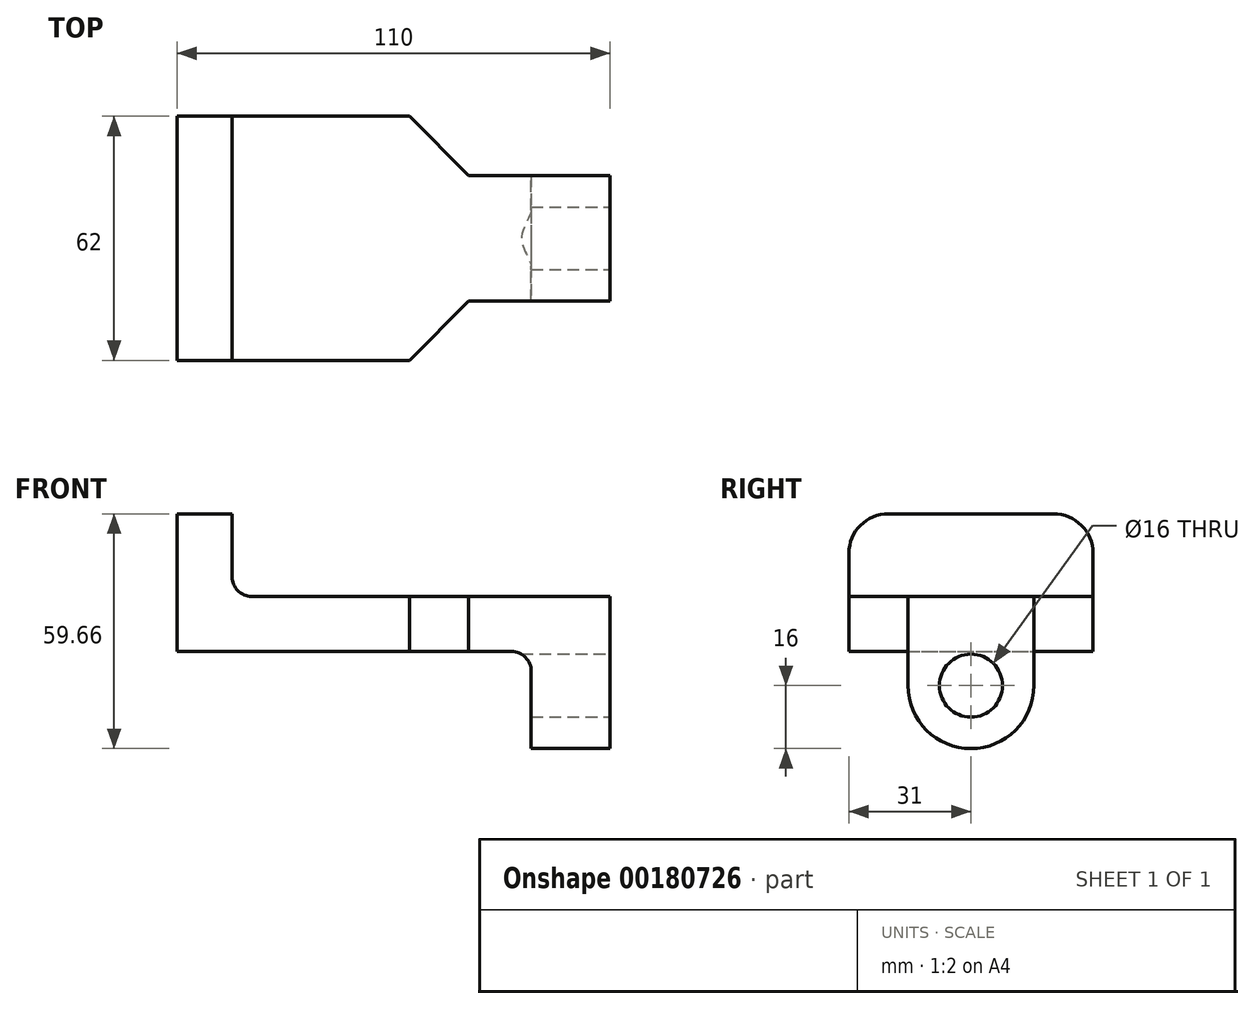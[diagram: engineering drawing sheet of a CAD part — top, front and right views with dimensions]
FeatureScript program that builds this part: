
annotation { "Feature Type Name" : "Feature", "Feature Type Description" : "" }
export const myFeature = defineFeature(function(context is Context, id is Id, definition is map)
    precondition{}
    {
        {
            var Q0;
            Q0=qCreatedBy(makeId("Front.planeOp"),FACE);
            var sketch = newSketch(context, id + "F0", { "sketchPlane" : qUnion([Q0])});
            skLineSegment(sketch, "E0", {"start": v(-90, 67.66) * mm, "end": v(-76, 67.66) * mm});
            skLineSegment(sketch, "E1", {"start": v(-76, 67.66) * mm, "end": v(-76, 46.66) * mm});
            skLineSegment(sketch, "E2", {"start": v(-76, 46.66) * mm, "end": v(20, 46.66) * mm});
            skLineSegment(sketch, "E3", {"start": v(20, 46.66) * mm, "end": v(20, 8) * mm});
            skLineSegment(sketch, "E4", {"start": v(20, 8) * mm, "end": v(0, 8) * mm});
            skLineSegment(sketch, "E5", {"start": v(0, 8) * mm, "end": v(0, 32.66) * mm});
            skLineSegment(sketch, "E6", {"start": v(0, 32.66) * mm, "end": v(-90, 32.66) * mm});
            skLineSegment(sketch, "E7", {"start": v(-90, 32.66) * mm, "end": v(-90, 67.66) * mm});
            skSolve(sketch);
        }
        {
            var Q0;
            Q0=makeQuery(id+"F0.imprint","IMPRINT",FACE,{"disambiguationData":[TD([[makeQuery(id+"F0.imprint","IMPRINT",EDGE,{"derivedFrom":sQuery(id+"F0.wireOp",EDGE,"E0")}),-1.0]])]});
            extrude(context, id + "F1", {"entities" : qUnion([Q0]), "depth" : 62 * mm});
        }
        {
            var Q0;
            Q0=makeQuery(id+"F1.opExtrude","CAP_EDGE",EDGE,{"disambiguationData":[OSD([sQuery(id+"F0.wireOp",EDGE,"E0")])],"isStart":false});
            var Q1;
            Q1=makeQuery(id+"F1.opExtrude","CAP_EDGE",EDGE,{"disambiguationData":[OSD([sQuery(id+"F0.wireOp",EDGE,"E0")])],"isStart":true});
            fillet(context, id + "F2", {"entities" : qUnion([Q0, Q1]), "radius" : 10 * mm, "tangentPropagation" : true, "allowEdgeOverflow" : false});
        }
        {
            var Q0;
            Q0=makeQuery(id+"F1.opExtrude","SWEPT_EDGE",EDGE,{"disambiguationData":[OSD([sQuery(id+"F0.wireOp",EDGE,"E1"),sQuery(id+"F0.wireOp",EDGE,"E2")])]});
            fillet(context, id + "F3", {"entities" : qUnion([Q0]), "radius" : 5 * mm, "tangentPropagation" : true, "allowEdgeOverflow" : false});
        }
        {
            var Q0;
            Q0=makeQuery(id+"F1.opExtrude","SWEPT_EDGE",EDGE,{"disambiguationData":[OSD([sQuery(id+"F0.wireOp",EDGE,"E5"),sQuery(id+"F0.wireOp",EDGE,"E6")])]});
            fillet(context, id + "F4", {"entities" : qUnion([Q0]), "radius" : 5 * mm, "tangentPropagation" : true, "allowEdgeOverflow" : false});
        }
        {
            var Q0;
            Q0=makeQuery(id+"F1.opExtrude","SWEPT_FACE",FACE,{"disambiguationData":[OSD([sQuery(id+"F0.wireOp",EDGE,"E2")])]});
            var sketch = newSketch(context, id + "F5", { "sketchPlane" : qUnion([Q0])});
            skLineSegment(sketch, "E8", {"start": v(20, -15) * mm, "end": v(20, -47) * mm});
            skLineSegment(sketch, "E9", {"start": v(-30.9, -62) * mm, "end": v(-89.9, -62) * mm});
            skLineSegment(sketch, "E10", {"start": v(-30.9, -62) * mm, "end": v(-15.9, -47) * mm});
            skLineSegment(sketch, "E11", {"start": v(20, -47) * mm, "end": v(-15.9, -47) * mm});
            skLineSegment(sketch, "E12", {"start": v(-30.9, 0) * mm, "end": v(-15.9, -15) * mm});
            skLineSegment(sketch, "E13", {"start": v(20, -15) * mm, "end": v(-15.9, -15) * mm});
            skLineSegment(sketch, "E14", {"start": v(-30.9, 0) * mm, "end": v(-30.9, 9.4) * mm});
            skLineSegment(sketch, "E15", {"start": v(-30.9, 9.4) * mm, "end": v(40.65, 7.07) * mm});
            skLineSegment(sketch, "E16", {"start": v(40.65, 7.07) * mm, "end": v(40.65, -48.81) * mm});
            skLineSegment(sketch, "E17", {"start": v(40.65, -48.81) * mm, "end": v(30.44, -74.08) * mm});
            skLineSegment(sketch, "E18", {"start": v(30.44, -74.08) * mm, "end": v(-28.45, -74.08) * mm});
            skLineSegment(sketch, "E19", {"start": v(-28.45, -74.08) * mm, "end": v(-30.9, -62) * mm});
            skSolve(sketch);
        }
        {
            var Q0;
            {var subQ0=sQuery(id+"F5.wireOp",EDGE,"E10");Q0=makeQuery(id+"F5.imprint","IMPRINT",FACE,{"disambiguationData":[TD([[makeQuery(id+"F5.imprint","IMPRINT",EDGE,{"derivedFrom":subQ0}),-1.0]])]});}
            var Q1;
            {var subQ0=sQuery(id+"F5.wireOp",EDGE,"E12");Q1=makeQuery(id+"F5.imprint","IMPRINT",FACE,{"disambiguationData":[TD([[makeQuery(id+"F5.imprint","IMPRINT",EDGE,{"derivedFrom":subQ0}),1.0]])]});}
            extrude(context, id + "F6", {"entities" : qUnion([Q0, Q1]), "operationType" : NewBodyOperationType.REMOVE, "oppositeDirection" : true, "depth" : 666 * mm});
        }
        {
            var Q0;
            Q0=makeQuery(id+"F6.boolean.opBoolean","INTERSECT",EDGE,{"derivedFrom":[makeQuery(id+"F1.opExtrude","SWEPT_FACE",FACE,{"disambiguationData":[OSD([sQuery(id+"F0.wireOp",EDGE,"E4")])]}),makeQuery(id+"F6.opExtrude","SWEPT_FACE",FACE,{"disambiguationData":[OSD([sQuery(id+"F5.wireOp",EDGE,"E11")])]})]});
            var Q1;
            Q1=makeQuery(id+"F6.boolean.opBoolean","INTERSECT",EDGE,{"derivedFrom":[makeQuery(id+"F1.opExtrude","SWEPT_FACE",FACE,{"disambiguationData":[OSD([sQuery(id+"F0.wireOp",EDGE,"E4")])]}),makeQuery(id+"F6.opExtrude","SWEPT_FACE",FACE,{"disambiguationData":[OSD([sQuery(id+"F5.wireOp",EDGE,"E13")])]})]});
            fillet(context, id + "F7", {"entities" : qUnion([Q0, Q1]), "radius" : 16 * mm, "tangentPropagation" : true, "allowEdgeOverflow" : false});
        }
        {
            var Q0;
            Q0=makeQuery(id+"F1.opExtrude","SWEPT_FACE",FACE,{"disambiguationData":[OSD([sQuery(id+"F0.wireOp",EDGE,"E3")])]});
            var sketch = newSketch(context, id + "F8", { "sketchPlane" : qUnion([Q0])});
            skCircle(sketch, "E20", {"center": v(-31, 24) * mm, "radius": 8 * mm});
            skSolve(sketch);
        }
        {
            var Q0;
            Q0=makeQuery(id+"F8.imprint","IMPRINT",FACE,{"disambiguationData":[TD([[makeQuery(id+"F8.imprint","IMPRINT",EDGE,{"derivedFrom":sQuery(id+"F8.wireOp",EDGE,"E20")}),1.0]])]});
            extrude(context, id + "F9", {"entities" : qUnion([Q0]), "operationType" : NewBodyOperationType.REMOVE, "oppositeDirection" : true, "depth" : 25 * mm});
        }
    });
